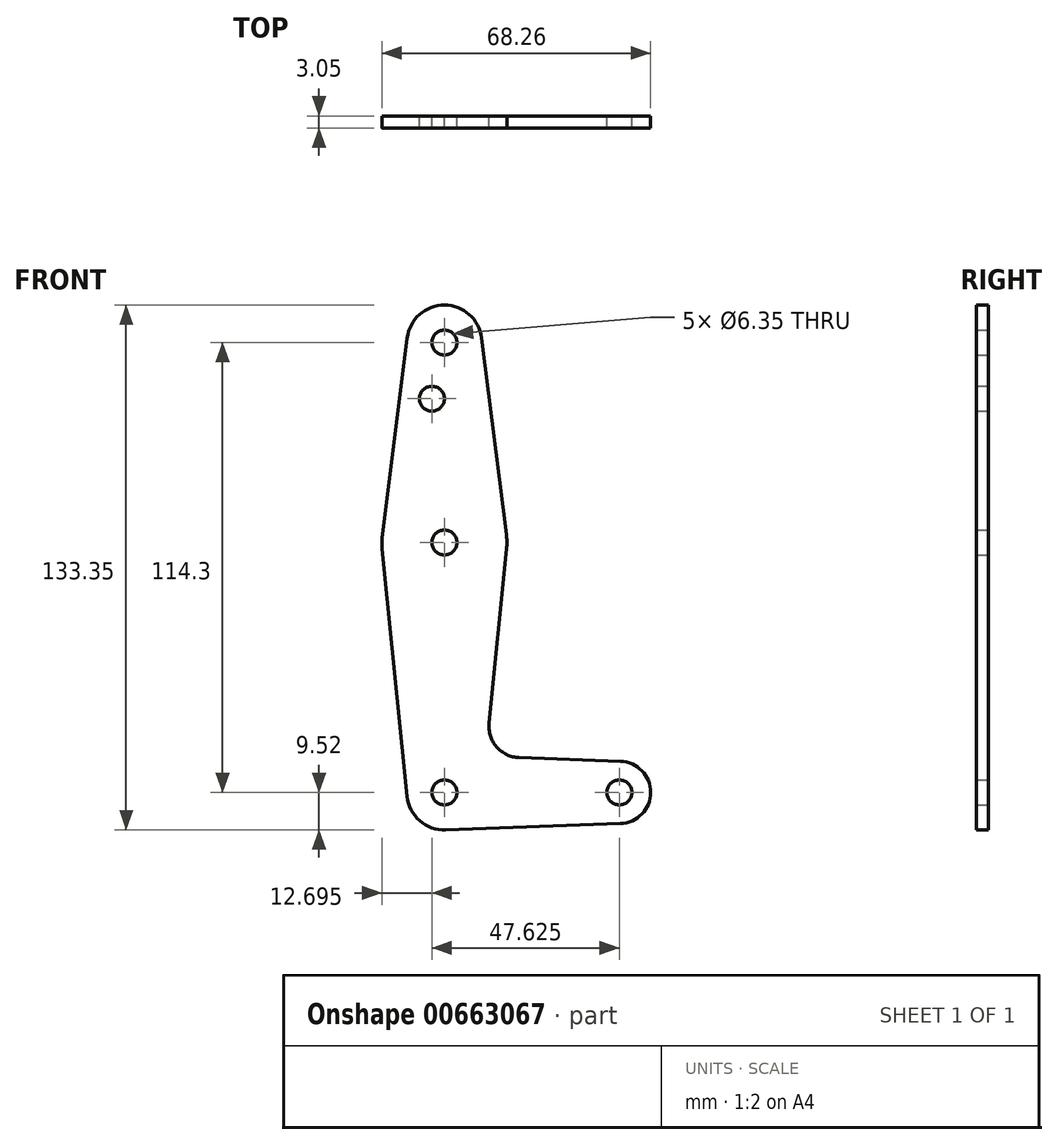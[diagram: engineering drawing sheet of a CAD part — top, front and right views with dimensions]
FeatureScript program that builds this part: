
annotation { "Feature Type Name" : "Feature", "Feature Type Description" : "" }
export const myFeature = defineFeature(function(context is Context, id is Id, definition is map)
    precondition{}
    {
        {
            var Q0;
            Q0=qCreatedBy(makeId("Front.planeOp"),FACE);
            var sketch = newSketch(context, id + "F0", { "sketchPlane" : qUnion([Q0])});
            skLineSegment(sketch, "E0", {"start": v(0, 0) * mm, "end": v(0, 114.3) * mm, "construction": true});
            skLineSegment(sketch, "E1", {"start": v(0, 0) * mm, "end": v(44.45, 0) * mm, "construction": true});
            skCircle(sketch, "E2", {"center": v(0, 114.3) * mm, "radius": 9.53 * mm});
            skCircle(sketch, "E3", {"center": v(0, 0) * mm, "radius": 9.53 * mm});
            skCircle(sketch, "E4", {"center": v(0, 63.5) * mm, "radius": 15.88 * mm});
            skCircle(sketch, "E5", {"center": v(44.45, 0) * mm, "radius": 7.94 * mm});
            skLineSegment(sketch, "E6", {"start": v(-15.75, 65.48) * mm, "end": v(-9.45, 115.5) * mm});
            skLineSegment(sketch, "E7", {"start": v(15.75, 65.48) * mm, "end": v(9.45, 115.5) * mm});
            skLineSegment(sketch, "E8", {"start": v(-15.8, 61.91) * mm, "end": v(-9.48, -0.95) * mm});
            skLineSegment(sketch, "E9", {"start": v(15.8, 61.91) * mm, "end": v(11.34, 17.6) * mm});
            skLineSegment(sketch, "E10", {"start": v(18.97, 8.85) * mm, "end": v(44.73, 7.93) * mm});
            skLineSegment(sketch, "E11", {"start": v(0.34, -9.52) * mm, "end": v(44.73, -7.93) * mm});
            skCircle(sketch, "E12", {"center": v(0, 114.3) * mm, "radius": 3.18 * mm});
            skCircle(sketch, "E13", {"center": v(0, 63.5) * mm, "radius": 3.18 * mm});
            skCircle(sketch, "E14", {"center": v(0, 0) * mm, "radius": 3.18 * mm});
            skCircle(sketch, "E15", {"center": v(44.45, 0) * mm, "radius": 3.18 * mm});
            skCircle(sketch, "E16", {"center": v(-3.18, 100.03) * mm, "radius": 3.18 * mm});
            skArc(sketch, "E17.filletArc", {"start": v(11.34, 17.6) * mm, "mid": v(13.26, 11.57) * mm, "end": v(18.97, 8.85) * mm});
            skSolve(sketch);
        }
        {
            var Q0;
            Q0 = qSketchRegion(id + "F0", true);
            extrude(context, id + "F1", {"entities" : qUnion([Q0]), "depth" : 3.05 * mm, "offsetDistance" : 25.4 * mm});
        }
    });
